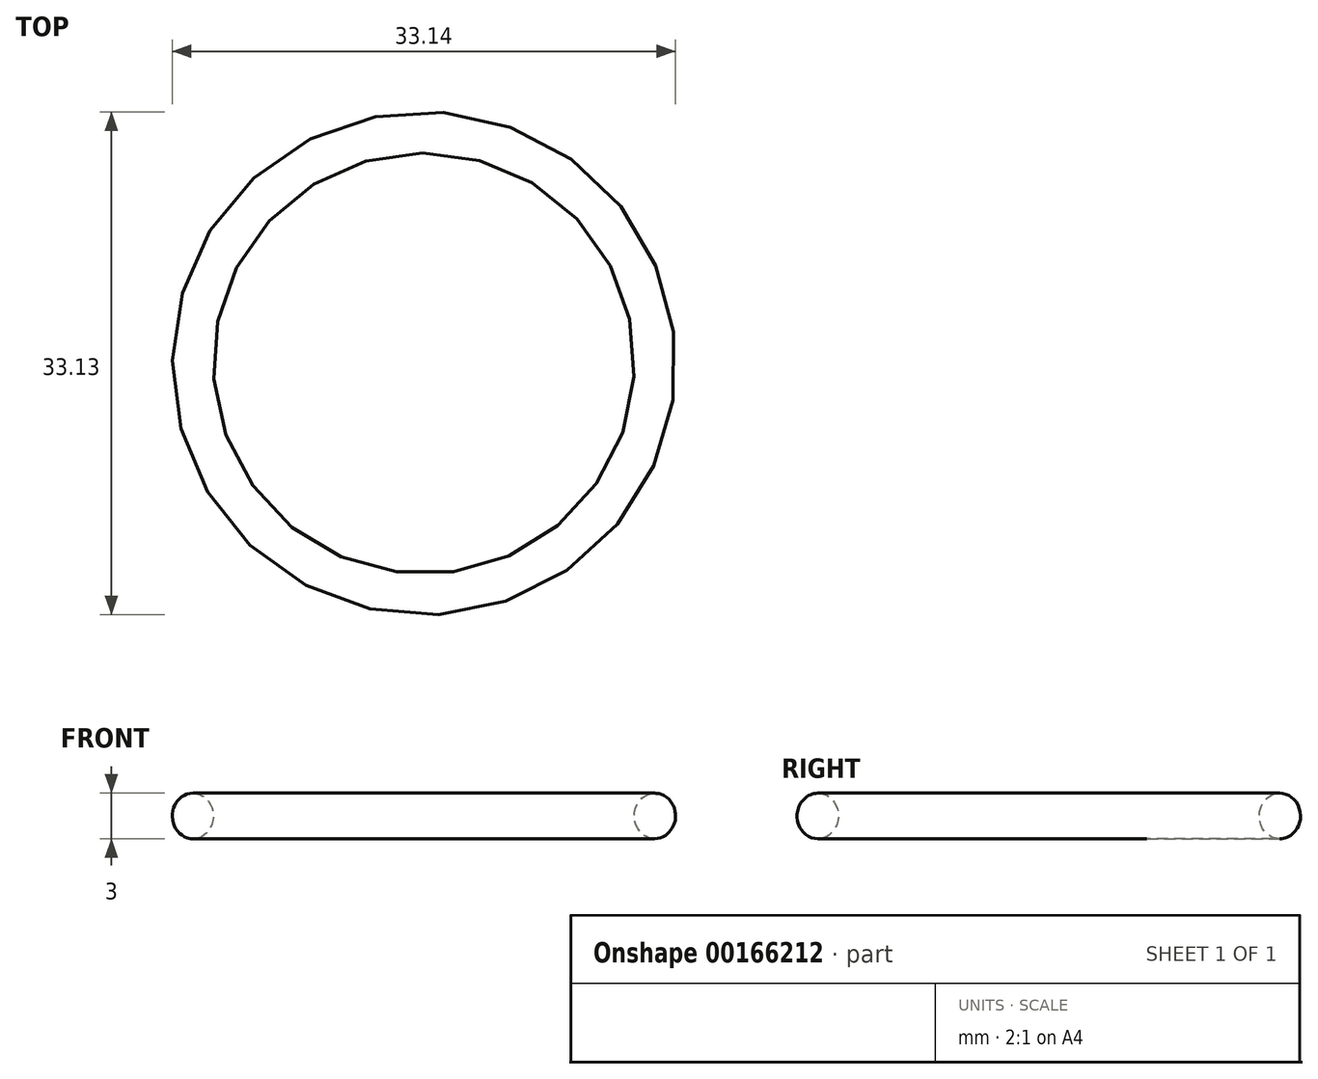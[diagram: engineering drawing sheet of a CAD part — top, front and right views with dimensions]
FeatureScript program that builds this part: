
annotation { "Feature Type Name" : "Feature", "Feature Type Description" : "" }
export const myFeature = defineFeature(function(context is Context, id is Id, definition is map)
    precondition{}
    {
        {
            var Q0;
            Q0=qCreatedBy(makeId("Front.planeOp"),FACE);
            var sketch = newSketch(context, id + "F0", { "sketchPlane" : qUnion([Q0])});
            skPoint(sketch, "E0.0", {"position": v(-51.5, 0) * mm});
            skCircle(sketch, "E1", {"center": v(-51.5, 0) * mm, "radius": 1.5 * mm});
            skSolve(sketch);
        }
        {
            var Q0;
            Q0=qCreatedBy(makeId("Top.planeOp"),FACE);
            var sketch = newSketch(context, id + "F1", { "sketchPlane" : qUnion([Q0])});
            skCircle(sketch, "E2", {"center": v(-37.74, 6.45) * mm, "radius": 15.27 * mm});
            skSolve(sketch);
        }
        {
            var Q0;
            Q0=makeQuery(id+"F0.imprint","IMPRINT",FACE,{"disambiguationData":[TD([[makeQuery(id+"F0.imprint","IMPRINT",EDGE,{"derivedFrom":sQuery(id+"F0.wireOp",EDGE,"E1")}),1.0]])]});
            var Q1;
            Q1=sQuery(id+"F1.wireOp",EDGE,"E2");
            sweep(context, id + "F2", {"profiles" : qUnion([Q0]), "path" : qUnion([Q1])});
        }
    });
